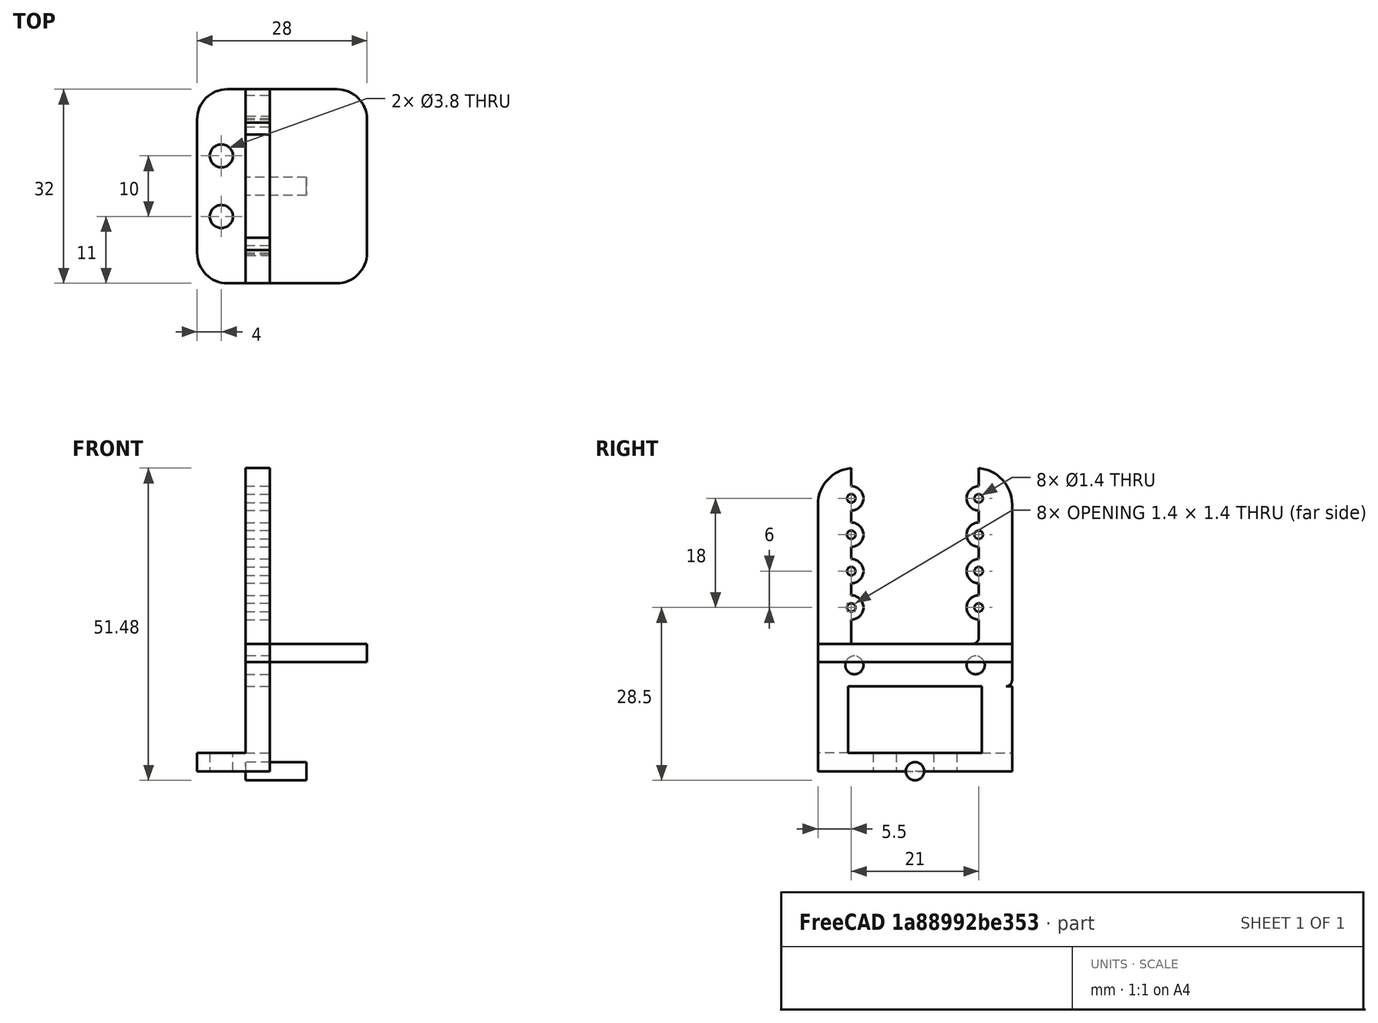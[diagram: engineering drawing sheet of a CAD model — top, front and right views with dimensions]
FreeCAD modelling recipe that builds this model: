
FCSTD DOCUMENT  (FreeCAD 0.20R29410 (Git))
Label: rpicam_stand
License: All rights reserved
LicenseURL: http://en.wikipedia.org/wiki/All_rights_reserved
objects: Part::Box×5, Part::MultiFuse×5, Part::Cylinder×4, Part::Fillet×4, Part::FeaturePython×3, Part::Cut×3, Part::Mirroring×2, Spreadsheet::Sheet×1, App::Part×1, Part::Refine×1
note: 26 computed .brp shape members not serialized (recipe doc carries the construction recipe); baked Part::Feature solids carry a one-line shape summary decoded from their .brp

FEATURE [Part::Cylinder] Cylinder  label="camera hole base"
  Angle = 360
  AttacherType = Attacher::AttachEngine3D
  FirstAngle = 0
  Height = 4
  Placement = pos=(0,0,0) rot=(0,1,0;1.5708rad)
  Radius = 2
  SecondAngle = 0
FEATURE [Part::FeaturePython] Array  label="camera hole base array"  # Draft array (typed FeaturePython)
  Angle = 360
  ArrayType = 0
  Axis = (0,0,1)
  Base = -> Cylinder
  Center = (0,0,0)
  Fuse = false
  IntervalAxis = (0,0,0)
  IntervalX = (1,0,0)
  IntervalY = (0,21,0)
  IntervalZ = (0,0,6)
  NumberPolar = 1
  NumberX = 1
  NumberY = 2
  NumberZ = 4
  Placement = pos=(0,-10.5,13) rot=(0,0,1;0rad)
  expr: .IntervalY.y = <<p>>.camera_hole_dist_y
  expr: .IntervalZ.z = <<p>>.camera_hole_dist_z / 2
  expr: .Placement.Base.y = -.IntervalY.y / 2
FEATURE [Spreadsheet::Sheet] Spreadsheet  label="p"
  cells = A1=camera_pcb_width; B1(camera_pcb_width)=25; A2=camera_pcb_height; B2(camera_pcb_height)=24; A3=camera_hole_dist_z; B3(camera_hole_dist_z)=12; A4=camera_hole_dist_y; B4(camera_hole_dist_y)=21; A5=slit_plate_width; B5(slit_plate_width)=59; A6=slit_plate_height; B6(slit_plate_height)=59; A7=slit_hole_height; B7(slit_hole_height)=40; A8=slit_hole_width; B8(slit_hole_width)=0.1
FEATURE [Part::Cylinder] Cylinder001  label="camera hole"
  Angle = 360
  AttacherType = Attacher::AttachEngine3D
  FirstAngle = 0
  Height = 4
  Placement = pos=(0,0,0) rot=(0,1,0;1.5708rad)
  Radius = 0.7
  SecondAngle = 0
FEATURE [Part::FeaturePython] Array001  label="camera hole array"  # Draft array (typed FeaturePython)
  Angle = 360
  ArrayType = 0
  Axis = (0,0,1)
  Base = -> Cylinder001
  Center = (0,0,0)
  Fuse = false
  IntervalAxis = (0,0,0)
  IntervalX = (1,0,0)
  IntervalY = (0,21,0)
  IntervalZ = (0,0,6)
  NumberPolar = 1
  NumberX = 1
  NumberY = 2
  NumberZ = 4
  Placement = pos=(0,-10.5,13) rot=(0,0,1;0rad)
  expr: .IntervalY.y = <<p>>.camera_hole_dist_y
  expr: .IntervalZ.z = <<p>>.camera_hole_dist_z / 2
  expr: .Placement.Base.y = -.IntervalY.y / 2
FEATURE [Part::Box] Box  label="camera plate"
  AttacherType = Attacher::AttachEngine3D
  Height = 36
  Length = 4
  Placement = pos=(0,-16,0) rot=(0,0,1;0rad)
  Width = 32
  expr: .Placement.Base.y = -Width / 2
FEATURE [Part::Box] Box001  label="camera plate hole"
  AttacherType = Attacher::AttachEngine3D
  Height = 74
  Length = 4
  Placement = pos=(0,-10.5,7) rot=(0,0,1;0rad)
  Width = 21
  expr: .Placement.Base.y = -Width / 2
  expr: Height = <<p>>.camera_pcb_height + 50
  expr: Width = <<p>>.camera_pcb_width - 4
FEATURE [Part::Fillet] Fillet001  label="camera plate fillet"
  Base = -> Box
  Edges = 2 edges r=6: [Edge10,Edge12]
FEATURE [Part::Cut] Cut001  label="camera plate cut"
  Base = -> Fillet001
  Tool = -> Box001
FEATURE [Part::Fillet] Fillet004  label="camera plate cut fillet"
  Base = -> Cut001
  Edges = 2 edges r=1: [Edge14,Edge21]
FEATURE [Part::MultiFuse] Fusion  label="camera plate fusion"
  Shapes = -> [Array,Fillet004]
FEATURE [Part::Box] Box002  label="side cube"
  AttacherType = Attacher::AttachEngine3D
  Height = 14
  Length = 4
  Placement = pos=(0,-16,0) rot=(0,0,1;0rad)
  Width = 5
  expr: .Placement.Base.y = <<camera plate>>.Placement.Base.y
  expr: Length = <<camera plate>>.Length
FEATURE [Part::Mirroring] Part__Mirroring  label="side cube (Mirror #1)"
  Base = (0,0,0)
  Normal = (0,1,0)
  Source = -> Box002
FEATURE [Part::Box] Box003  label="bottom cube"
  AttacherType = Attacher::AttachEngine3D
  Height = 3
  Length = 12
  Placement = pos=(-8,-16,0) rot=(0,0,1;0rad)
  Width = 32
  expr: .Placement.Base.x = <<side cube>>.Length - Length
  expr: .Placement.Base.y = -Width / 2
  expr: Width = <<camera plate>>.Width
FEATURE [Part::Cylinder] Cylinder002  label="bottom bolt hole"
  Angle = 360
  AttacherType = Attacher::AttachEngine3D
  FirstAngle = 0
  Height = 10
  Placement = pos=(0,-5,0) rot=(0,0,1;0rad)
  Radius = 1.9
  SecondAngle = 0
FEATURE [Part::Mirroring] Part__Mirroring001  label="bottom bolt hole (Mirror #2)"
  Base = (0,0,0)
  Normal = (0,1,0)
  Source = -> Cylinder002
FEATURE [Part::Fillet] Fillet  label="bottom cube fillet"
  Base = -> Box003
  Edges = 2 edges r=5: [Edge1,Edge3]
FEATURE [Part::MultiFuse] Fusion001  label="bottom stand fusion"
  Shapes = -> [Part__Mirroring,Box002,Fillet]
FEATURE [Part::MultiFuse] Fusion002  label="bottom hole fusion"
  Placement = pos=(-4,0,0) rot=(0,0,1;0rad)
  Shapes = -> [Part__Mirroring001,Cylinder002]
  expr: .Placement.Base.x = -<<bottom cube>>.Length + 8mm
FEATURE [Part::Cut] Cut002  label="bottom stand cut"
  Base = -> Fusion001
  Tool = -> Fusion002
FEATURE [Part::Box] Box004  label="middle cube"
  AttacherType = Attacher::AttachEngine3D
  Height = 3
  Length = 20
  Placement = pos=(0,-16,18) rot=(0,0,1;0rad)
  Width = 32
  expr: .Placement.Base.y = -Width / 2
  expr: .Placement.Base.z = <<side cube>>.Height + <<camera plate hole>>.Placement.Base.z - Height
  expr: Width = <<camera plate>>.Width
FEATURE [Part::Fillet] Fillet005  label="moddle cube fillet"
  Base = -> Box004
  Edges = 2 edges r=5: [Edge5,Edge7]
FEATURE [Part::Cylinder] Cylinder003  label="middle bolt hole"
  Angle = 360
  AttacherType = Attacher::AttachEngine3D
  FirstAngle = 0
  Height = 10
  Placement = pos=(0,0,0) rot=(0,1,0;1.5708rad)
  Radius = 1.5
  SecondAngle = 0
FEATURE [Part::FeaturePython] Array002  label="middle bolt hole array"  # Draft array (typed FeaturePython)
  AlwaysSyncPlacement = false
  Angle = 360
  ArrayType = 0
  Axis = (0,0,1)
  Base = -> Cylinder003
  Center = (0,0,0)
  Count = 2
  ExpandArray = false
  Fuse = false
  IntervalAxis = (0,0,0)
  IntervalX = (100,0,0)
  IntervalY = (0,20,0)
  IntervalZ = (0,0,100)
  NumberCircles = 3
  NumberPolar = 5
  NumberX = 1
  NumberY = 2
  NumberZ = 1
  Placement = pos=(-5,-10,3.5) rot=(0,0,1;0rad)
  PlacementList = 2 placements: [(0,0,0),(0,20,0)]
  RadialDistance = 50
  ScaleList = (2) [(1,1,1),(1,1,1)]
  Symmetry = 1
  TangentialDistance = 25
  expr: .Placement.Base.y = -.IntervalY.y / 2
  expr: .Placement.Base.z = <<camera plate hole>>.Placement.Base.z / 2
FEATURE [Part::MultiFuse] Fusion003002  label="camera hole fusion"
  Shapes = -> [Array001,Array002]
FEATURE [Part::Cut] Cut  label="camera holder cut"
  Base = -> Fusion
  Placement = pos=(0,0,14) rot=(0,0,1;0rad)
  Tool = -> Fusion003002
  expr: .Placement.Base.z = <<side cube>>.Height
FEATURE [Part::MultiFuse] Fusion003  label="camera holder with stand"
  Shapes = -> [Cut002,Cut]
FEATURE [App::Part] Part
  Group = -> [Fusion003]
  Origin = -> Origin
FEATURE [Part::Refine] Fusion003001  label="camera holder with stand001"
  Source = -> Fusion003
